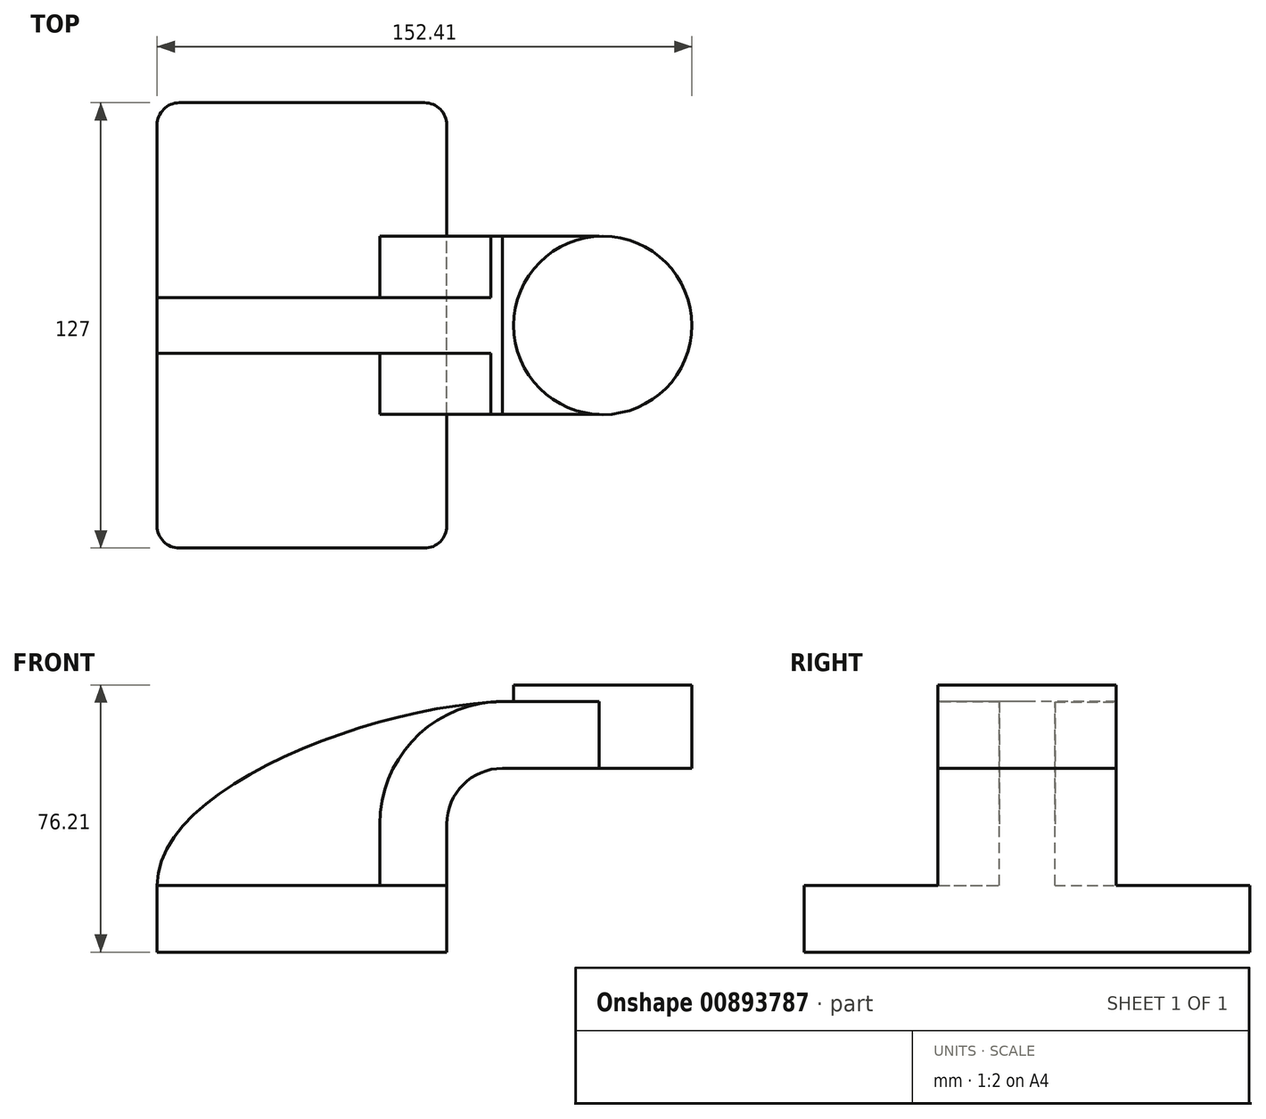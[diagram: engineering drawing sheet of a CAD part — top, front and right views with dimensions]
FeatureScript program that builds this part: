
annotation { "Feature Type Name" : "Feature", "Feature Type Description" : "" }
export const myFeature = defineFeature(function(context is Context, id is Id, definition is map)
    precondition{}
    {
        {
            var Q0;
            Q0=qCreatedBy(makeId("Front.planeOp"),FACE);
            var sketch = newSketch(context, id + "F0", { "sketchPlane" : qUnion([Q0])});
            skLineSegment(sketch, "E0.bottom", {"start": v(-41.27, -9.53) * mm, "end": v(41.28, -9.53) * mm});
            skLineSegment(sketch, "E0.top", {"start": v(-41.28, 9.53) * mm, "end": v(41.28, 9.53) * mm});
            skLineSegment(sketch, "E0.left", {"start": v(-41.28, -9.53) * mm, "end": v(-41.28, 9.53) * mm});
            skLineSegment(sketch, "E0.right", {"start": v(41.28, -9.53) * mm, "end": v(41.28, 9.53) * mm});
            skPoint(sketch, "E0.middle", {"position": v(0, 0) * mm});
            skLineSegment(sketch, "E1.bottom", {"start": v(60.32, 38.1) * mm, "end": v(111.12, 38.1) * mm});
            skLineSegment(sketch, "E1.top", {"start": v(60.32, 66.67) * mm, "end": v(111.12, 66.67) * mm});
            skLineSegment(sketch, "E1.left", {"start": v(60.32, 38.1) * mm, "end": v(60.32, 66.67) * mm});
            skLineSegment(sketch, "E1.right", {"start": v(111.12, 38.1) * mm, "end": v(111.12, 66.67) * mm});
            skPoint(sketch, "E1.middle", {"position": v(85.72, 52.39) * mm});
            skLineSegment(sketch, "E2", {"start": v(41.28, 9.53) * mm, "end": v(41.28, 27) * mm});
            skArc(sketch, "E3", {"start": v(41.27, 27) * mm, "mid": v(45.92, 38.23) * mm, "end": v(57.15, 42.88) * mm});
            skLineSegment(sketch, "E4", {"start": v(57.15, 42.88) * mm, "end": v(111.15, 42.88) * mm});
            skLineSegment(sketch, "E5.0", {"start": v(57.15, 61.93) * mm, "end": v(109.55, 61.93) * mm});
            skArc(sketch, "E5.1", {"start": v(22.22, 27) * mm, "mid": v(32.45, 51.7) * mm, "end": v(57.15, 61.93) * mm});
            skLineSegment(sketch, "E5.2", {"start": v(22.23, 9.53) * mm, "end": v(22.23, 27) * mm});
            skLineSegment(sketch, "E6", {"start": v(85.7, 42.88) * mm, "end": v(85.7, 66.67) * mm});
            skFitSpline(sketch, "E7", {"points": [v(-41.28, 9.53) * mm, v(57.15, 61.93) * mm], "startDerivative": vector(-0.39, 84.14) * mm, "endDerivative": vector(109.74, 3.42) * mm});
            skSolve(sketch);
        }
        {
            var Q0;
            {var subQ1=sQuery(id+"F0.wireOp",EDGE,"E2");Q0=makeQuery(id+"F0.imprint","IMPRINT",FACE,{"disambiguationData":[TD([[makeQuery(id+"F0.imprint","IMPRINT",EDGE,{"derivedFrom":subQ1}),1.0]])]});}
            var Q1;
            {var subQ0=sQuery(id+"F0.wireOp",EDGE,"E4");var subQ1=sQuery(id+"F0.wireOp",EDGE,"E1.left");var subQ2=makeQuery(id+"F0.imprint","INTERSECT",VERTEX,{"derivedFrom":[subQ1,subQ0]});Q1=makeQuery(id+"F0.imprint","IMPRINT",FACE,{"disambiguationData":[TD([[makeQuery(id+"F0.imprint","IMPRINT",EDGE,{"disambiguationData":[TD([[subQ2,-1.0]])],"derivedFrom":subQ1}),-1.0]])]});}
            extrude(context, id + "F1", {"entities" : qUnion([Q0, Q1]), "endBound" : BoundingType.SYMMETRIC, "depth" : 50.8 * mm, "offsetDistance" : 25.4 * mm});
        }
        {
            var Q0;
            Q0=makeQuery(id+"F0.imprint","IMPRINT",FACE,{"disambiguationData":[TD([[makeQuery(id+"F0.imprint","IMPRINT",EDGE,{"derivedFrom":sQuery(id+"F0.wireOp",EDGE,"E0.bottom")}),1.0]])]});
            extrude(context, id + "F2", {"entities" : qUnion([Q0]), "operationType" : NewBodyOperationType.ADD, "endBound" : BoundingType.SYMMETRIC, "depth" : 127 * mm, "offsetDistance" : 25.4 * mm});
        }
        {
            var Q0;
            {var subQ3=sQuery(id+"F0.wireOp",EDGE,"E5.2");Q0=makeQuery(id+"F0.imprint","IMPRINT",FACE,{"disambiguationData":[TD([[makeQuery(id+"F0.imprint","IMPRINT",EDGE,{"derivedFrom":subQ3}),1.0]])]});}
            extrude(context, id + "F3", {"entities" : qUnion([Q0]), "operationType" : NewBodyOperationType.ADD, "endBound" : BoundingType.SYMMETRIC, "depth" : 15.88 * mm, "offsetDistance" : 25.4 * mm});
        }
        {
            var Q0;
            {var subQ4=sQuery(id+"F0.wireOp",EDGE,"E1.right");var subQ5=sQuery(id+"F0.wireOp",EDGE,"E1.top");var subQ6=makeQuery(id+"F0.imprint","INTERSECT",VERTEX,{"derivedFrom":[subQ5,subQ4]});Q0=makeQuery(id+"F0.imprint","IMPRINT",FACE,{"disambiguationData":[TD([[makeQuery(id+"F0.imprint","IMPRINT",EDGE,{"disambiguationData":[TD([[subQ6,1.0]])],"derivedFrom":subQ5}),-1.0]])]});}
            var Q1;
            Q1=sQuery(id+"F0.wireOp",EDGE,"E6");
            revolve(context, id + "F4", {"operationType" : NewBodyOperationType.ADD, "surfaceOperationType" : NewSurfaceOperationType.NEW, "entities" : qUnion([Q0]), "axis" : qUnion([Q1]), "revolveType" : RevolveType.FULL});
        }
        {
            var Q0;
            Q0=makeQuery(id+"F2.opExtrude","CAP_EDGE",EDGE,{"disambiguationData":[OSD([sQuery(id+"F0.wireOp",EDGE,"E0.right")])],"isStart":false});
            var Q1;
            Q1=makeQuery(id+"F2.opExtrude","CAP_EDGE",EDGE,{"disambiguationData":[OSD([sQuery(id+"F0.wireOp",EDGE,"E0.left")])],"isStart":false});
            var Q2;
            Q2=makeQuery(id+"F2.opExtrude","CAP_EDGE",EDGE,{"disambiguationData":[OSD([sQuery(id+"F0.wireOp",EDGE,"E0.right")])],"isStart":true});
            var Q3;
            Q3=makeQuery(id+"F2.opExtrude","CAP_EDGE",EDGE,{"disambiguationData":[OSD([sQuery(id+"F0.wireOp",EDGE,"E0.left")])],"isStart":true});
            fillet(context, id + "F5", {"entities" : qUnion([Q0, Q1, Q2, Q3]), "radius" : 6.35 * mm, "tangentPropagation" : true, "allowEdgeOverflow" : false});
        }
    });
